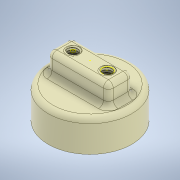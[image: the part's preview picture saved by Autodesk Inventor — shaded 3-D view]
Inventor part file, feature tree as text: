
AUTODESK INVENTOR PART (.ipt)
format: ipt  version: 2020 (Build 240168000, 168)  size: 1,436,160 bytes
history: mixed  units: in
note: dims shown in document units (in); Inventor stores cm internally (conversion verified against a paired STEP export)
features: sketch x7, extrude x2, hole x2, thread x2, revolve x2, helix x2, fillet x1, other x1, imported_body x1
ambient origin geometry x8: Origin, YZ Plane, XZ Plane, XY Plane, X Axis, Y Axis, Z Axis, Center Point
bodies: Solid1 (imported_parasolid), Solid2 (imported_parasolid), Solid3 (imported_parasolid)
feature tree (20):
  extrude  "Extrusion1"  Depth=0.3937in
  extrude  "Extrusion2"  Depth=0.1969in TaperAngle=0.0deg
  sketch  "Sketch3"  dims[d6=0.211in d7=0.25in d8=0.4375in d9=0.25in d10=0.5635in d11=0.25in d12=0.0in]
  hole  "Hole1"  [1 undecoded]
  hole  "Hole2"  [1 undecoded]
  thread  "Thread1"  [1 undecoded]
  thread  "Thread2"  [1 undecoded]
  revolve  "Revolution1"  [1 undecoded]
  helix  "Coil1"  [1 undecoded]
  revolve  "Revolution2"  [1 undecoded]
  helix  "Coil2"  [1 undecoded]
  fillet  "Fillet1"  Radius=0.0787in
  sketch  "Sketch1"  dims[d0=0.9843in d1=0.3937in]
  sketch  "Sketch2"  dims[d2=0.325in d3=0.0in d4=0.1969in d5=0.0in]
  sketch  "Sketch4"  dims[d13=0.0625in d14=0.25in d15=0.4375in d16=0.25in d17=0.5635in d18=0.25in d19=0.0in d20=0.25in d21=0.0in]
  sketch  "Sketch5"  dims[d22=0.25in d23=0.0in d24=0.3779in d25=0.0057in d26=0.0057in d29=0.0357in d31=0.3779in]
  sketch  "Sketch6"  dims[d33=0.0in]
  sketch  "Sketch7"  dims[d34=0.0358in d35=0.3214in d36=0.3937in d37=0.0in d38=0.0in d39=0.0in d40=0.0in d41=0.0in d42=0.3779in d43=0.0057in d44=0.0057in d47=0.0357in d49=0.3779in d51=0.0in d52=0.0358in d53=0.3214in d54=0.3937in d55=0.0in d56=0.0in d57=0.0in d58=0.0in d59=0.0in d60=0.0787in]
  other  "tube_inlets_rear"
  imported_body  NMx_Import_Brep_tag  [imported B-rep: ~14 faces, bbox_mm=None]
note: 8 required parameter values undecoded (feature->parameter linkage not recoverable at this tier; creation-order binding heuristic only, values carry confidence <= 0.55)